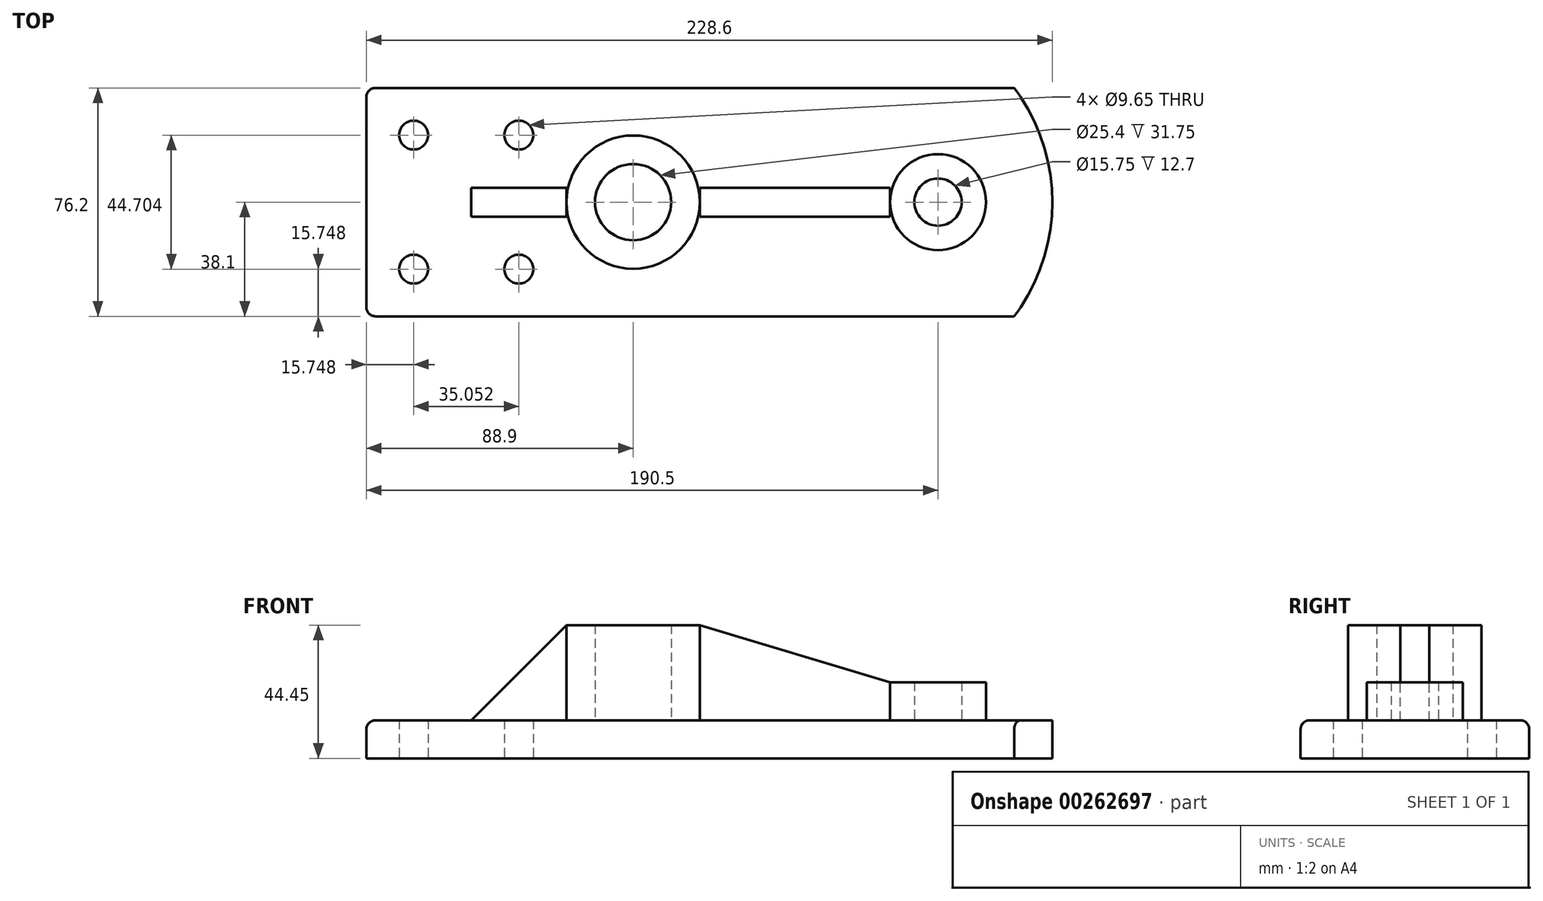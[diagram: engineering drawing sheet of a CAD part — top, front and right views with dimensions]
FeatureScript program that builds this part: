
annotation { "Feature Type Name" : "Feature", "Feature Type Description" : "" }
export const myFeature = defineFeature(function(context is Context, id is Id, definition is map)
    precondition{}
    {
        {
            var Q0;
            Q0=qCreatedBy(makeId("Top.planeOp"),FACE);
            var sketch = newSketch(context, id + "F0", { "sketchPlane" : qUnion([Q0])});
            skLineSegment(sketch, "E0.bottom", {"start": v(-50.8, 38.1) * mm, "end": v(139.7, 38.1) * mm});
            skLineSegment(sketch, "E0.top", {"start": v(-50.8, -38.1) * mm, "end": v(139.7, -38.1) * mm});
            skLineSegment(sketch, "E0.left", {"start": v(-50.8, 38.1) * mm, "end": v(-50.8, -38.1) * mm});
            skCircle(sketch, "E1", {"center": v(-35.05, 22.35) * mm, "radius": 4.83 * mm});
            skCircle(sketch, "E2", {"center": v(-35.05, -22.35) * mm, "radius": 4.83 * mm});
            skCircle(sketch, "E3", {"center": v(0, -22.35) * mm, "radius": 4.83 * mm});
            skCircle(sketch, "E4", {"center": v(0, 22.35) * mm, "radius": 4.83 * mm});
            skLineSegment(sketch, "E5", {"start": v(-50.8, 0) * mm, "end": v(139.7, 0) * mm});
            skPoint(sketch, "E5.endSnap0", {"position": v(139.7, 0) * mm});
            skArc(sketch, "E6", {"start": v(165.1, -38.1) * mm, "mid": v(177.8, 0) * mm, "end": v(165.1, 38.1) * mm});
            skLineSegment(sketch, "E7", {"start": v(139.7, 38.1) * mm, "end": v(165.1, 38.1) * mm});
            skLineSegment(sketch, "E8", {"start": v(139.7, -38.1) * mm, "end": v(165.1, -38.1) * mm});
            skSolve(sketch);
        }
        {
            var Q0;
            Q0 = qSketchRegion(id + "F0", true);
            extrude(context, id + "F1", {"entities" : qUnion([Q0]), "depth" : 12.7 * mm});
        }
        {
            var Q0;
            Q0=makeQuery(id+"F1.opExtrude","CAP_FACE",FACE,{"disambiguationData":[OSD([sQuery(id+"F0.wireOp",EDGE,"E0.bottom"),sQuery(id+"F0.wireOp",EDGE,"E0.top"),sQuery(id+"F0.wireOp",EDGE,"E0.left"),sQuery(id+"F0.wireOp",EDGE,"E1"),sQuery(id+"F0.wireOp",EDGE,"E2"),sQuery(id+"F0.wireOp",EDGE,"E3"),sQuery(id+"F0.wireOp",EDGE,"E4"),sQuery(id+"F0.wireOp",EDGE,"eYIRnpEZ-Zvnu-5pc5-L3IG-GRDK7aWC2Vdf")])],"isStart":false});
            var sketch = newSketch(context, id + "F2", { "sketchPlane" : qUnion([Q0])});
            skCircle(sketch, "E9", {"center": v(38.1, 0) * mm, "radius": 12.7 * mm});
            skPoint(sketch, "E10.middle", {"position": v(0, 0) * mm});
            skCircle(sketch, "E11", {"center": v(38.1, 0) * mm, "radius": 22.23 * mm});
            skSolve(sketch);
        }
        {
            var Q0;
            Q0 = qSketchRegion(id + "F2", true);
            extrude(context, id + "F3", {"entities" : qUnion([Q0]), "operationType" : NewBodyOperationType.ADD, "depth" : 31.75 * mm});
        }
        {
            var Q0;
            {var subQ0=sQuery(id+"F0.wireOp",EDGE,"E1");var subQ1=sQuery(id+"F0.wireOp",EDGE,"E0.left");var subQ2=sQuery(id+"F0.wireOp",EDGE,"E8");var subQ3=sQuery(id+"F0.wireOp",EDGE,"E0.top");var subQ4=sQuery(id+"F0.wireOp",EDGE,"E7");var subQ5=sQuery(id+"F0.wireOp",EDGE,"E0.bottom");var subQ6=sQuery(id+"F0.wireOp",EDGE,"E2");var subQ7=sQuery(id+"F0.wireOp",EDGE,"E3");var subQ8=sQuery(id+"F0.wireOp",EDGE,"E4");var subQ9=sQuery(id+"F0.wireOp",EDGE,"E6");Q0=makeQuery(id+"F3.boolean.opBoolean","SPLIT",FACE,{"disambiguationData":[TD([makeQuery(id+"F1.opExtrude","SWEPT_FACE",FACE,{"disambiguationData":[OSD([subQ1])]})])],"derivedFrom":makeQuery(id+"F1.opExtrude","CAP_FACE",FACE,{"disambiguationData":[OSD([subQ5,subQ3,subQ1,subQ0,subQ6,subQ7,subQ8,subQ9,subQ4,subQ2])],"isStart":false})});}
            var sketch = newSketch(context, id + "F4", { "sketchPlane" : qUnion([Q0])});
            skCircle(sketch, "E12", {"center": v(139.7, 0) * mm, "radius": 16 * mm});
            skCircle(sketch, "E13", {"center": v(139.7, 0) * mm, "radius": 7.87 * mm});
            skSolve(sketch);
        }
        {
            var Q0;
            Q0 = qSketchRegion(id + "F4", true);
            extrude(context, id + "F5", {"entities" : qUnion([Q0]), "operationType" : NewBodyOperationType.ADD, "depth" : 12.7 * mm});
        }
        {
            var Q0;
            Q0=qCreatedBy(makeId("Front.planeOp"),FACE);
            var sketch = newSketch(context, id + "F6", { "sketchPlane" : qUnion([Q0])});
            skLineSegment(sketch, "E14", {"start": v(15.88, 12.7) * mm, "end": v(15.88, 44.45) * mm});
            skLineSegment(sketch, "E15.0", {"start": v(-15.88, 12.7) * mm, "end": v(15.88, 12.7) * mm});
            skLineSegment(sketch, "E16", {"start": v(60.33, 44.45) * mm, "end": v(60.33, 12.7) * mm});
            skLineSegment(sketch, "E17", {"start": v(123.7, 12.7) * mm, "end": v(123.7, 25.4) * mm});
            skLineSegment(sketch, "E18", {"start": v(15.88, 44.45) * mm, "end": v(-15.88, 12.7) * mm});
            skLineSegment(sketch, "E19", {"start": v(60.32, 44.45) * mm, "end": v(123.7, 25.4) * mm});
            skPoint(sketch, "E20.orphan", {"position": v(-50.8, 12.7) * mm});
            skLineSegment(sketch, "E21.trimOffspring", {"start": v(60.33, 12.7) * mm, "end": v(123.7, 12.7) * mm});
            skPoint(sketch, "E22.orphan", {"position": v(165.1, 12.7) * mm});
            skSolve(sketch);
        }
        {
            var Q0;
            Q0 = qSketchRegion(id + "F6", true);
            extrude(context, id + "F7", {"entities" : qUnion([Q0]), "endBound" : BoundingType.SYMMETRIC, "depth" : 9.65 * mm});
        }
        {
            var Q0;
            Q0=makeQuery(id+"F1.opExtrude","CAP_EDGE",EDGE,{"disambiguationData":[OSD([sQuery(id+"F0.wireOp",EDGE,"E0.top"),sQuery(id+"F0.wireOp",EDGE,"E8")])],"isStart":false});
            var Q1;
            Q1=makeQuery(id+"F1.opExtrude","CAP_EDGE",EDGE,{"disambiguationData":[OSD([sQuery(id+"F0.wireOp",EDGE,"E0.left")])],"isStart":false});
            var Q2;
            Q2=makeQuery(id+"F1.opExtrude","CAP_EDGE",EDGE,{"disambiguationData":[OSD([sQuery(id+"F0.wireOp",EDGE,"E0.bottom"),sQuery(id+"F0.wireOp",EDGE,"E7")])],"isStart":false});
            var Q3;
            Q3=makeQuery(id+"F1.opExtrude","SWEPT_EDGE",EDGE,{"disambiguationData":[OSD([sQuery(id+"F0.wireOp",EDGE,"E0.top"),sQuery(id+"F0.wireOp",EDGE,"E0.left")])]});
            var Q4;
            Q4=makeQuery(id+"F1.opExtrude","SWEPT_EDGE",EDGE,{"disambiguationData":[OSD([sQuery(id+"F0.wireOp",EDGE,"E0.bottom"),sQuery(id+"F0.wireOp",EDGE,"E0.left")])]});
            var Q5;
            Q5=makeQuery(id+"F5.opExtrude","CAP_EDGE",EDGE,{"disambiguationData":[OSD([sQuery(id+"F4.wireOp",EDGE,"E12")])],"isStart":true});
            var Q6;
            Q6=makeQuery(id+"F3.opExtrude","CAP_EDGE",EDGE,{"disambiguationData":[OSD([sQuery(id+"F2.wireOp",EDGE,"E11")])],"isStart":true});
            fillet(context, id + "F8", {"entities" : qUnion([Q0, Q1, Q2, Q3, Q4, Q5, Q6]), "radius" : 3.05 * mm, "tangentPropagation" : true, "allowEdgeOverflow" : false});
        }
    });
